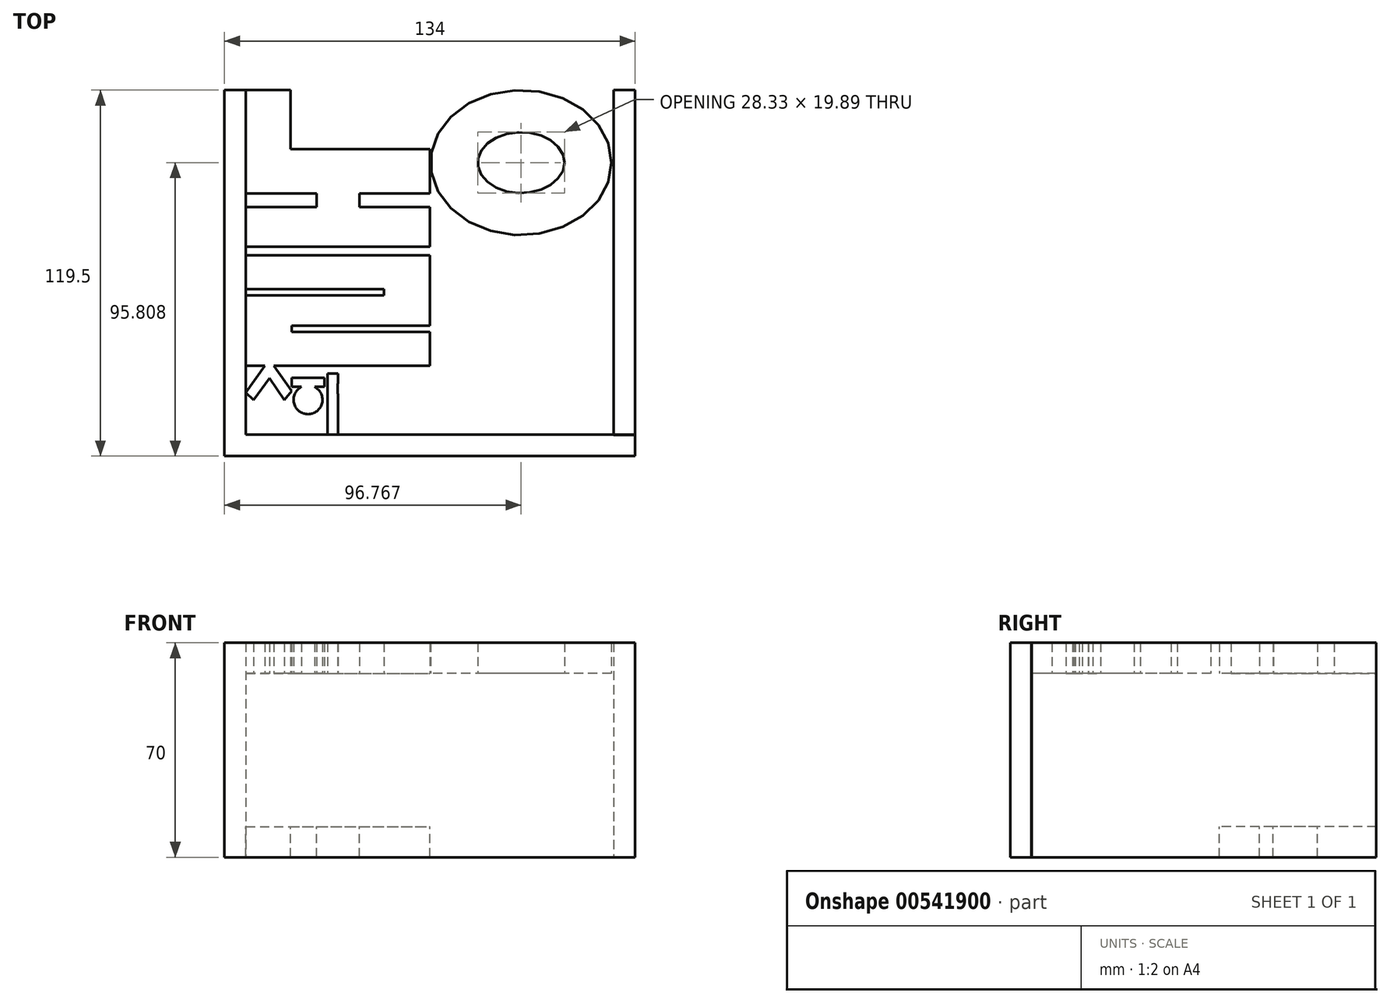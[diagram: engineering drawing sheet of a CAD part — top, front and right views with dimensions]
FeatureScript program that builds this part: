
annotation { "Feature Type Name" : "Feature", "Feature Type Description" : "" }
export const myFeature = defineFeature(function(context is Context, id is Id, definition is map)
    precondition{}
    {
        {
            var Q0;
            Q0=qCreatedBy(makeId("Top.planeOp"),FACE);
            var sketch = newSketch(context, id + "F0", { "sketchPlane" : qUnion([Q0])});
            skLineSegment(sketch, "E0.bottom", {"start": v(-60, 45) * mm, "end": v(60, 45) * mm});
            skLineSegment(sketch, "E0.top", {"start": v(-60, -45) * mm, "end": v(60, -45) * mm});
            skLineSegment(sketch, "E0.left", {"start": v(-60, 45) * mm, "end": v(-60, -45) * mm});
            skLineSegment(sketch, "E0.right", {"start": v(60, 45) * mm, "end": v(60, -45) * mm});
            skLineSegment(sketch, "E1.top", {"start": v(-60, -67.5) * mm, "end": v(60, -67.5) * mm});
            skLineSegment(sketch, "E1.left", {"start": v(-60, -45) * mm, "end": v(-60, -67.5) * mm});
            skLineSegment(sketch, "E1.right", {"start": v(60, -45) * mm, "end": v(60, -67.5) * mm});
            skLineSegment(sketch, "E2", {"start": v(-45, -45) * mm, "end": v(-45, -67.5) * mm});
            skLineSegment(sketch, "E3", {"start": v(-30, -45) * mm, "end": v(-30, -67.5) * mm});
            skLineSegment(sketch, "E4", {"start": v(-15, -45) * mm, "end": v(-15, -67.5) * mm});
            skLineSegment(sketch, "E5", {"start": v(15, -45) * mm, "end": v(15, -67.5) * mm});
            skLineSegment(sketch, "E6", {"start": v(30, -45) * mm, "end": v(30, -67.5) * mm});
            skLineSegment(sketch, "E7", {"start": v(45, -45) * mm, "end": v(45, -67.5) * mm});
            skLineSegment(sketch, "E8.bottom", {"start": v(-45.5, 45) * mm, "end": v(0, 45) * mm});
            skLineSegment(sketch, "E8.top", {"start": v(-45.5, 25.78) * mm, "end": v(0, 25.78) * mm});
            skLineSegment(sketch, "E8.left", {"start": v(-45.5, 45) * mm, "end": v(-45.5, 25.78) * mm});
            skLineSegment(sketch, "E8.right", {"start": v(0, 45) * mm, "end": v(0, 25.78) * mm});
            skLineSegment(sketch, "E9.bottom", {"start": v(-60, 11.28) * mm, "end": v(-36.94, 11.28) * mm});
            skLineSegment(sketch, "E9.top", {"start": v(-60, 6.78) * mm, "end": v(-36.94, 6.78) * mm});
            skLineSegment(sketch, "E9.left", {"start": v(-60, 11.28) * mm, "end": v(-60, 6.78) * mm});
            skLineSegment(sketch, "E9.right", {"start": v(-36.94, 11.28) * mm, "end": v(-36.94, 6.78) * mm});
            skLineSegment(sketch, "E10.bottom", {"start": v(-22.94, 11.28) * mm, "end": v(0, 11.28) * mm});
            skLineSegment(sketch, "E10.top", {"start": v(-22.94, 6.78) * mm, "end": v(0, 6.78) * mm});
            skLineSegment(sketch, "E10.left", {"start": v(-22.94, 11.28) * mm, "end": v(-22.94, 6.78) * mm});
            skLineSegment(sketch, "E10.right", {"start": v(0, 11.28) * mm, "end": v(0, 6.78) * mm});
            skLineSegment(sketch, "E11.bottom", {"start": v(-60, -6.22) * mm, "end": v(0, -6.22) * mm});
            skLineSegment(sketch, "E11.top", {"start": v(-60, -9) * mm, "end": v(0, -9) * mm});
            skLineSegment(sketch, "E11.left", {"start": v(-60, -6.22) * mm, "end": v(-60, -9) * mm});
            skLineSegment(sketch, "E11.right", {"start": v(0, -6.22) * mm, "end": v(0, -9) * mm});
            skLineSegment(sketch, "E12.bottom", {"start": v(-60, -20) * mm, "end": v(-15, -20) * mm});
            skLineSegment(sketch, "E12.top", {"start": v(-60, -22) * mm, "end": v(-15, -22) * mm});
            skLineSegment(sketch, "E12.left", {"start": v(-60, -20) * mm, "end": v(-60, -22) * mm});
            skLineSegment(sketch, "E12.right", {"start": v(-15, -20) * mm, "end": v(-15, -22) * mm});
            skLineSegment(sketch, "E13.bottom", {"start": v(-45, -32) * mm, "end": v(0, -32) * mm});
            skLineSegment(sketch, "E13.top", {"start": v(-45, -34) * mm, "end": v(0, -34) * mm});
            skLineSegment(sketch, "E13.left", {"start": v(-45, -32) * mm, "end": v(-45, -34) * mm});
            skLineSegment(sketch, "E13.right", {"start": v(0, -32) * mm, "end": v(0, -34) * mm});
            skEllipse(sketch, "E14", {"center": v(29.77, 21.3) * mm, "majorRadius": 29.48 * mm, "minorRadius": 23.67 * mm, "majorAxis": v(1, 0)});
            skEllipse(sketch, "E15", {"center": v(29.77, 21.3) * mm, "majorRadius": 14.16 * mm, "minorRadius": 9.95 * mm, "majorAxis": v(1, 0)});
            skLineSegment(sketch, "E16.bottom", {"start": v(0, 0.28) * mm, "end": v(60, 0.28) * mm});
            skLineSegment(sketch, "E16.top", {"start": v(0, -15.86) * mm, "end": v(60, -15.86) * mm});
            skLineSegment(sketch, "E16.left", {"start": v(0, 0.28) * mm, "end": v(0, -15.86) * mm});
            skLineSegment(sketch, "E16.right", {"start": v(60, 0.28) * mm, "end": v(60, -15.86) * mm});
            skLineSegment(sketch, "E17.bottom", {"start": v(13.88, -15.86) * mm, "end": v(26.86, -15.86) * mm});
            skLineSegment(sketch, "E17.top", {"start": v(13.88, -45) * mm, "end": v(26.86, -45) * mm});
            skLineSegment(sketch, "E17.left", {"start": v(13.88, -15.86) * mm, "end": v(13.88, -45) * mm});
            skLineSegment(sketch, "E17.right", {"start": v(26.86, -15.86) * mm, "end": v(26.86, -45) * mm});
            skLineSegment(sketch, "E18.bottom", {"start": v(36.88, -15.86) * mm, "end": v(49.4, -15.86) * mm});
            skLineSegment(sketch, "E18.top", {"start": v(36.88, -45) * mm, "end": v(49.4, -45) * mm});
            skLineSegment(sketch, "E18.left", {"start": v(36.88, -15.86) * mm, "end": v(36.88, -45) * mm});
            skLineSegment(sketch, "E18.right", {"start": v(49.4, -15.86) * mm, "end": v(49.4, -45) * mm});
            skLineSegment(sketch, "E19", {"start": v(0, 45) * mm, "end": v(0, -45) * mm});
            skLineSegment(sketch, "E20", {"start": v(0.02, -67.07) * mm, "end": v(0, -45) * mm});
            skLineSegment(sketch, "E21.bottom", {"start": v(-60, 45) * mm, "end": v(-67, 45) * mm});
            skLineSegment(sketch, "E21.top", {"start": v(-60, -67.5) * mm, "end": v(-67, -67.5) * mm});
            skLineSegment(sketch, "E21.left", {"start": v(-60, 45) * mm, "end": v(-60, -67.5) * mm});
            skLineSegment(sketch, "E21.right", {"start": v(-67, 45) * mm, "end": v(-67, -67.5) * mm});
            skLineSegment(sketch, "E22.bottom", {"start": v(60, 45) * mm, "end": v(67, 45) * mm});
            skLineSegment(sketch, "E22.top", {"start": v(60, -67.62) * mm, "end": v(67, -67.62) * mm});
            skLineSegment(sketch, "E22.left", {"start": v(60, 45) * mm, "end": v(60, -67.62) * mm});
            skLineSegment(sketch, "E22.right", {"start": v(67, 45) * mm, "end": v(67, -67.62) * mm});
            skLineSegment(sketch, "E23.bottom", {"start": v(-67, -67.5) * mm, "end": v(67, -67.5) * mm});
            skLineSegment(sketch, "E23.top", {"start": v(-67, -74.5) * mm, "end": v(67, -74.5) * mm});
            skLineSegment(sketch, "E23.left", {"start": v(-67, -67.5) * mm, "end": v(-67, -74.5) * mm});
            skLineSegment(sketch, "E23.right", {"start": v(67, -67.5) * mm, "end": v(67, -74.5) * mm});
            skLineSegment(sketch, "E24.bottom", {"start": v(-60, -56.25) * mm, "end": v(-45, -56.25) * mm});
            skLineSegment(sketch, "E24.top", {"start": v(-60, -60.3) * mm, "end": v(-45, -60.3) * mm});
            skLineSegment(sketch, "E24.left", {"start": v(-60, -56.25) * mm, "end": v(-60, -60.3) * mm});
            skLineSegment(sketch, "E24.right", {"start": v(-45, -56.25) * mm, "end": v(-45, -60.3) * mm});
            skLineSegment(sketch, "E25.bottom", {"start": v(-54.3, -60.3) * mm, "end": v(-50.04, -60.3) * mm});
            skLineSegment(sketch, "E25.top", {"start": v(-54.3, -67.5) * mm, "end": v(-50.04, -67.5) * mm});
            skLineSegment(sketch, "E25.left", {"start": v(-54.3, -60.3) * mm, "end": v(-54.3, -67.5) * mm});
            skLineSegment(sketch, "E25.right", {"start": v(-50.04, -60.3) * mm, "end": v(-50.04, -67.5) * mm});
            skLineSegment(sketch, "E26", {"start": v(-60, -53.78) * mm, "end": v(-53.87, -45) * mm});
            skLineSegment(sketch, "E27", {"start": v(-53.87, -45) * mm, "end": v(-50.9, -45) * mm});
            skLineSegment(sketch, "E28", {"start": v(-50.9, -45) * mm, "end": v(-45, -53.22) * mm});
            skLineSegment(sketch, "E29", {"start": v(-45, -53.22) * mm, "end": v(-47.5, -56.25) * mm});
            skLineSegment(sketch, "E30", {"start": v(-47.5, -56.25) * mm, "end": v(-52.26, -49.02) * mm});
            skLineSegment(sketch, "E31", {"start": v(-52.26, -49.02) * mm, "end": v(-57.55, -56.25) * mm});
            skLineSegment(sketch, "E32", {"start": v(-57.55, -56.25) * mm, "end": v(-60, -53.78) * mm});
            skLineSegment(sketch, "E33.bottom", {"start": v(-41.24, -45) * mm, "end": v(-38.44, -45) * mm});
            skLineSegment(sketch, "E33.top", {"start": v(-41.24, -48.82) * mm, "end": v(-38.44, -48.82) * mm});
            skLineSegment(sketch, "E33.left", {"start": v(-41.24, -45) * mm, "end": v(-41.24, -48.82) * mm});
            skLineSegment(sketch, "E33.right", {"start": v(-38.44, -45) * mm, "end": v(-38.44, -48.82) * mm});
            skLineSegment(sketch, "E34.bottom", {"start": v(-45.05, -48.92) * mm, "end": v(-34.33, -48.92) * mm});
            skLineSegment(sketch, "E34.top", {"start": v(-45.05, -51.93) * mm, "end": v(-34.33, -51.93) * mm});
            skLineSegment(sketch, "E34.left", {"start": v(-45.05, -48.92) * mm, "end": v(-45.05, -51.93) * mm});
            skLineSegment(sketch, "E34.right", {"start": v(-34.33, -48.92) * mm, "end": v(-34.33, -51.93) * mm});
            skCircle(sketch, "E35", {"center": v(-39.74, -56.13) * mm, "radius": 4.71 * mm});
            skLineSegment(sketch, "E36.bottom", {"start": v(-45, -61.85) * mm, "end": v(-32.8, -61.85) * mm});
            skLineSegment(sketch, "E36.top", {"start": v(-45, -64.7) * mm, "end": v(-32.8, -64.7) * mm});
            skLineSegment(sketch, "E36.left", {"start": v(-45, -61.85) * mm, "end": v(-45, -64.7) * mm});
            skLineSegment(sketch, "E36.right", {"start": v(-32.8, -61.85) * mm, "end": v(-32.8, -64.7) * mm});
            skLineSegment(sketch, "E37.bottom", {"start": v(-33.4, -47.56) * mm, "end": v(-30, -47.56) * mm});
            skLineSegment(sketch, "E37.top", {"start": v(-33.4, -67.5) * mm, "end": v(-30, -67.5) * mm});
            skLineSegment(sketch, "E37.left", {"start": v(-33.4, -47.56) * mm, "end": v(-33.4, -67.5) * mm});
            skLineSegment(sketch, "E37.right", {"start": v(-30, -47.56) * mm, "end": v(-30, -67.5) * mm});
            skLineSegment(sketch, "E38.bottom", {"start": v(-26.13, -47.92) * mm, "end": v(-23.5, -47.92) * mm});
            skLineSegment(sketch, "E38.top", {"start": v(-26.13, -51.6) * mm, "end": v(-23.5, -51.6) * mm});
            skLineSegment(sketch, "E38.left", {"start": v(-26.13, -47.92) * mm, "end": v(-26.13, -51.6) * mm});
            skLineSegment(sketch, "E38.right", {"start": v(-23.5, -47.92) * mm, "end": v(-23.5, -51.6) * mm});
            skLineSegment(sketch, "E39.bottom", {"start": v(-30.06, -50.9) * mm, "end": v(-19.94, -50.9) * mm});
            skLineSegment(sketch, "E39.top", {"start": v(-30.06, -54.1) * mm, "end": v(-19.94, -54.1) * mm});
            skLineSegment(sketch, "E39.left", {"start": v(-30.06, -50.9) * mm, "end": v(-30.06, -54.1) * mm});
            skLineSegment(sketch, "E39.right", {"start": v(-19.94, -50.9) * mm, "end": v(-19.94, -54.1) * mm});
            skCircle(sketch, "E40", {"center": v(-24.52, -58.04) * mm, "radius": 3.66 * mm});
            skSolve(sketch);
        }
        {
            var Q0;
            {var subQ9=sQuery(id+"F0.wireOp",EDGE,"E8.top");Q0=makeQuery(id+"F0.imprint","IMPRINT",FACE,{"disambiguationData":[TD([[makeQuery(id+"F0.imprint","IMPRINT",EDGE,{"derivedFrom":subQ9}),-1.0]])]});}
            var Q1;
            {var subQ8=sQuery(id+"F0.wireOp",EDGE,"E11.top");Q1=makeQuery(id+"F0.imprint","IMPRINT",FACE,{"disambiguationData":[TD([[makeQuery(id+"F0.imprint","IMPRINT",EDGE,{"derivedFrom":subQ8}),-1.0]])]});}
            var Q2;
            {var subQ6=sQuery(id+"F0.wireOp",EDGE,"E16.right");Q2=makeQuery(id+"F0.imprint","IMPRINT",FACE,{"disambiguationData":[TD([[makeQuery(id+"F0.imprint","IMPRINT",EDGE,{"derivedFrom":subQ6}),-1.0]])]});}
            var Q3;
            Q3=makeQuery(id+"F0.imprint","IMPRINT",FACE,{"disambiguationData":[TD([[makeQuery(id+"F0.imprint","IMPRINT",EDGE,{"derivedFrom":sQuery(id+"F0.wireOp",EDGE,"E15")}),-1.0]])]});
            var Q4;
            {var subQ0=sQuery(id+"F0.wireOp",EDGE,"E16.bottom");var subQ1=sQuery(id+"F0.wireOp",EDGE,"E14");var subQ2=makeQuery(id+"F0.imprint","INTERSECT",VERTEX,{"disambiguationData":[OD(0.0)],"derivedFrom":[subQ1,subQ0]});Q4=makeQuery(id+"F0.imprint","IMPRINT",FACE,{"disambiguationData":[TD([[makeQuery(id+"F0.imprint","IMPRINT",EDGE,{"disambiguationData":[TD([[subQ2,-1.0]])],"derivedFrom":subQ1}),1.0]])]});}
            var Q5;
            Q5=makeQuery(id+"F0.imprint","IMPRINT",FACE,{"disambiguationData":[TD([[makeQuery(id+"F0.imprint","IMPRINT",EDGE,{"derivedFrom":sQuery(id+"F0.wireOp",EDGE,"E17.bottom")}),-1.0]])]});
            var Q6;
            Q6=makeQuery(id+"F0.imprint","IMPRINT",FACE,{"disambiguationData":[TD([[makeQuery(id+"F0.imprint","IMPRINT",EDGE,{"derivedFrom":sQuery(id+"F0.wireOp",EDGE,"E18.bottom")}),-1.0]])]});
            var Q7;
            {var subQ8=sQuery(id+"F0.wireOp",EDGE,"E17.bottom");Q7=makeQuery(id+"F0.imprint","IMPRINT",FACE,{"disambiguationData":[TD([[makeQuery(id+"F0.imprint","IMPRINT",EDGE,{"derivedFrom":subQ8}),1.0]])]});}
            var Q8;
            Q8=makeQuery(id+"F0.imprint","IMPRINT",FACE,{"disambiguationData":[TD([[makeQuery(id+"F0.imprint","IMPRINT",EDGE,{"derivedFrom":sQuery(id+"F0.wireOp",EDGE,"E26")}),-1.0]])]});
            var Q9;
            {var subQ0=sQuery(id+"F0.wireOp",EDGE,"E24.left");Q9=makeQuery(id+"F0.imprint","IMPRINT",FACE,{"disambiguationData":[TD([[makeQuery(id+"F0.imprint","IMPRINT",EDGE,{"derivedFrom":subQ0}),1.0]])]});}
            var Q10;
            Q10=makeQuery(id+"F0.imprint","IMPRINT",FACE,{"disambiguationData":[TD([[makeQuery(id+"F0.imprint","IMPRINT",EDGE,{"derivedFrom":sQuery(id+"F0.wireOp",EDGE,"E25.bottom")}),-1.0]])]});
            var Q11;
            {var subQ0=sQuery(id+"F0.wireOp",EDGE,"E35");var subQ1=sQuery(id+"F0.wireOp",EDGE,"E34.top");var subQ2=makeQuery(id+"F0.imprint","INTERSECT",VERTEX,{"disambiguationData":[OD(0.0)],"derivedFrom":[subQ1,subQ0]});Q11=makeQuery(id+"F0.imprint","IMPRINT",FACE,{"disambiguationData":[TD([[makeQuery(id+"F0.imprint","IMPRINT",EDGE,{"disambiguationData":[TD([[subQ2,-1.0]])],"derivedFrom":subQ1}),-1.0]])]});}
            var Q12;
            {var subQ0=sQuery(id+"F0.wireOp",EDGE,"E34.right");Q12=makeQuery(id+"F0.imprint","IMPRINT",FACE,{"disambiguationData":[TD([[makeQuery(id+"F0.imprint","IMPRINT",EDGE,{"derivedFrom":subQ0}),-1.0]])]});}
            var Q13;
            {var subQ0=sQuery(id+"F0.wireOp",EDGE,"E35");var subQ1=sQuery(id+"F0.wireOp",EDGE,"E34.top");var subQ2=makeQuery(id+"F0.imprint","INTERSECT",VERTEX,{"disambiguationData":[OD(0.0)],"derivedFrom":[subQ1,subQ0]});Q13=makeQuery(id+"F0.imprint","IMPRINT",FACE,{"disambiguationData":[TD([[makeQuery(id+"F0.imprint","IMPRINT",EDGE,{"disambiguationData":[TD([[subQ2,-1.0]])],"derivedFrom":subQ1}),1.0]])]});}
            var Q14;
            Q14=makeQuery(id+"F0.imprint","IMPRINT",FACE,{"disambiguationData":[TD([[makeQuery(id+"F0.imprint","IMPRINT",EDGE,{"derivedFrom":sQuery(id+"F0.wireOp",EDGE,"E33.bottom")}),-1.0]])]});
            var Q15;
            {var subQ14=sQuery(id+"F0.wireOp",EDGE,"E36.right");Q15=makeQuery(id+"F0.imprint","IMPRINT",FACE,{"disambiguationData":[TD([[makeQuery(id+"F0.imprint","IMPRINT",EDGE,{"derivedFrom":subQ14}),1.0]])]});}
            var Q16;
            {var subQ0=sQuery(id+"F0.wireOp",EDGE,"E36.right");Q16=makeQuery(id+"F0.imprint","IMPRINT",FACE,{"disambiguationData":[TD([[makeQuery(id+"F0.imprint","IMPRINT",EDGE,{"derivedFrom":subQ0}),-1.0]])]});}
            var Q17;
            {var subQ0=sQuery(id+"F0.wireOp",EDGE,"E36.left");Q17=makeQuery(id+"F0.imprint","IMPRINT",FACE,{"disambiguationData":[TD([[makeQuery(id+"F0.imprint","IMPRINT",EDGE,{"derivedFrom":subQ0}),1.0]])]});}
            extrude(context, id + "F1", {"entities" : qUnion([Q0, Q1, Q2, Q3, Q4, Q5, Q6, Q7, Q8, Q9, Q10, Q11, Q12, Q13, Q14, Q15, Q16, Q17]), "depth" : 35 * mm, "offsetDistance" : 25 * mm, "hasSecondDirection" : true, "secondDirectionOppositeDirection" : false, "secondDirectionDepth" : 25 * mm});
        }
        {
            var Q0;
            {var subQ9=sQuery(id+"F0.wireOp",EDGE,"E21.bottom");Q0=makeQuery(id+"F0.imprint","IMPRINT",FACE,{"disambiguationData":[TD([[makeQuery(id+"F0.imprint","IMPRINT",EDGE,{"derivedFrom":subQ9}),1.0]])]});}
            var Q1;
            {var subQ9=sQuery(id+"F0.wireOp",EDGE,"E22.top");Q1=makeQuery(id+"F0.imprint","IMPRINT",FACE,{"disambiguationData":[TD([[makeQuery(id+"F0.imprint","IMPRINT",EDGE,{"derivedFrom":subQ9}),-1.0]])]});}
            var Q2;
            {var subQ4=sQuery(id+"F0.wireOp",EDGE,"E22.bottom");Q2=makeQuery(id+"F0.imprint","IMPRINT",FACE,{"disambiguationData":[TD([[makeQuery(id+"F0.imprint","IMPRINT",EDGE,{"derivedFrom":subQ4}),-1.0]])]});}
            extrude(context, id + "F2", {"entities" : qUnion([Q0, Q1, Q2]), "endBound" : BoundingType.SYMMETRIC, "depth" : 70 * mm, "offsetDistance" : 25 * mm});
        }
        {
            var Q0;
            Q0=makeQuery(id+"F1.opExtrude","CAP_FACE",FACE,{"disambiguationData":[OSD([sQuery(id+"F0.wireOp",EDGE,"E0.bottom"),sQuery(id+"F0.wireOp",EDGE,"E0.top"),sQuery(id+"F0.wireOp",EDGE,"E8.top"),sQuery(id+"F0.wireOp",EDGE,"E8.left"),sQuery(id+"F0.wireOp",EDGE,"E9.bottom"),sQuery(id+"F0.wireOp",EDGE,"E9.top"),sQuery(id+"F0.wireOp",EDGE,"E9.right"),sQuery(id+"F0.wireOp",EDGE,"E10.bottom"),sQuery(id+"F0.wireOp",EDGE,"E10.top"),sQuery(id+"F0.wireOp",EDGE,"E10.left"),sQuery(id+"F0.wireOp",EDGE,"E11.bottom"),sQuery(id+"F0.wireOp",EDGE,"E11.top"),sQuery(id+"F0.wireOp",EDGE,"E12.bottom"),sQuery(id+"F0.wireOp",EDGE,"E12.top"),sQuery(id+"F0.wireOp",EDGE,"E12.right"),sQuery(id+"F0.wireOp",EDGE,"E13.bottom"),sQuery(id+"F0.wireOp",EDGE,"E13.top"),sQuery(id+"F0.wireOp",EDGE,"E13.left"),sQuery(id+"F0.wireOp",EDGE,"E14"),sQuery(id+"F0.wireOp",EDGE,"E15"),sQuery(id+"F0.wireOp",EDGE,"E16.bottom"),sQuery(id+"F0.wireOp",EDGE,"E16.top"),sQuery(id+"F0.wireOp",EDGE,"E17.top"),sQuery(id+"F0.wireOp",EDGE,"E17.left"),sQuery(id+"F0.wireOp",EDGE,"E17.right"),sQuery(id+"F0.wireOp",EDGE,"E18.top"),sQuery(id+"F0.wireOp",EDGE,"E18.left"),sQuery(id+"F0.wireOp",EDGE,"E18.right"),sQuery(id+"F0.wireOp",EDGE,"E19"),sQuery(id+"F0.wireOp",EDGE,"E21.left"),sQuery(id+"F0.wireOp",EDGE,"E22.left")])],"isStart":true});
            extrude(context, id + "F3", {"entities" : qUnion([Q0]), "depth" : 60 * mm, "offsetDistance" : 25 * mm, "hasSecondDirection" : true, "secondDirectionOppositeDirection" : false, "secondDirectionDepth" : 50 * mm});
        }
    });
